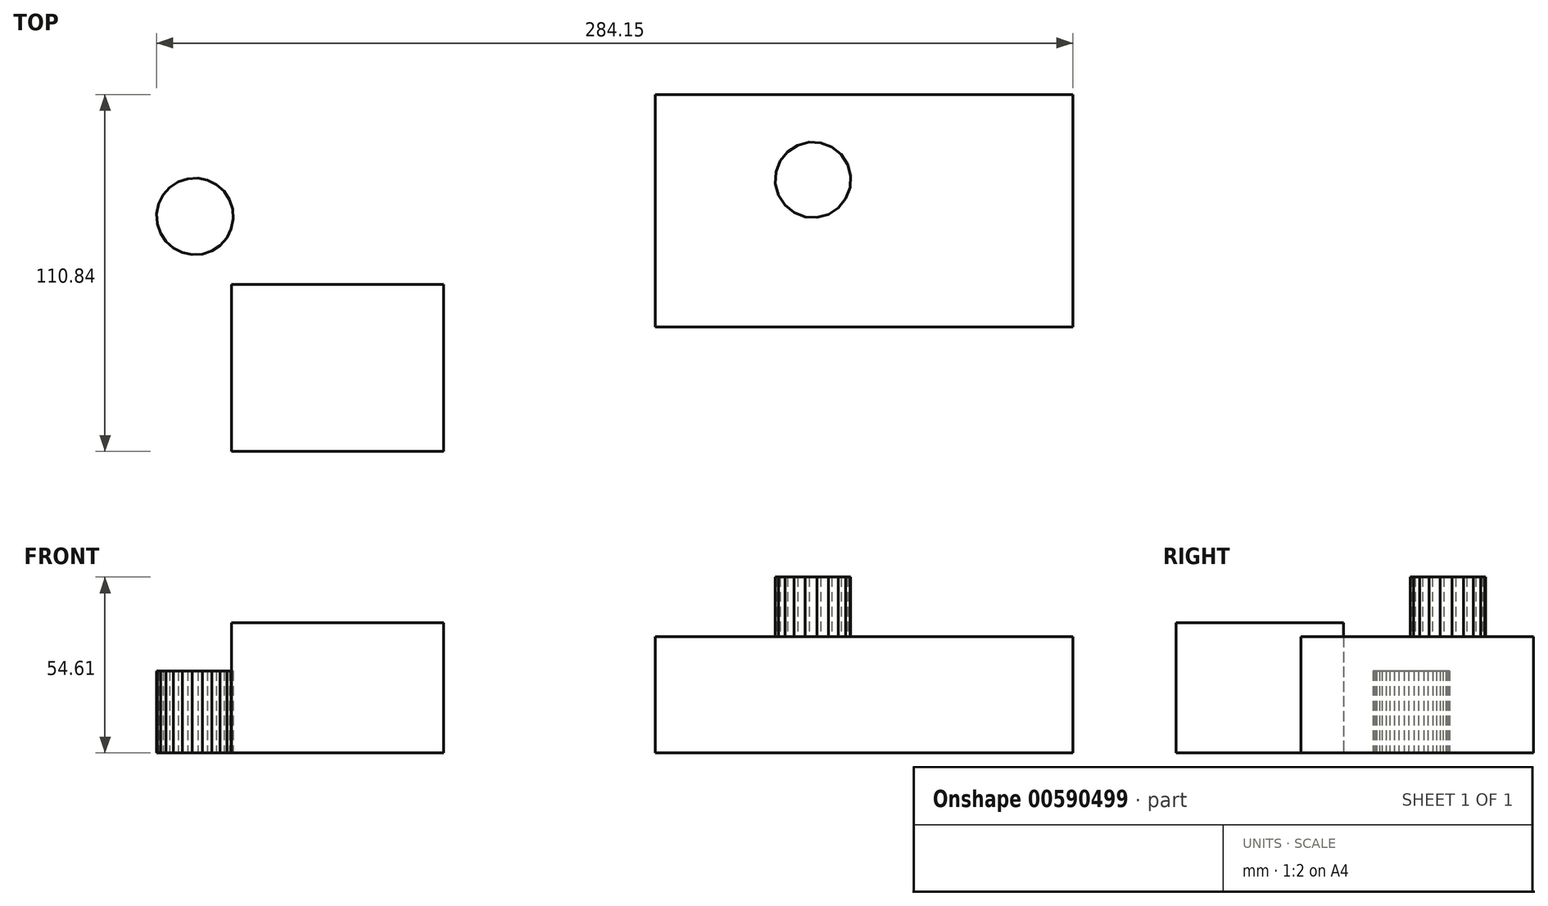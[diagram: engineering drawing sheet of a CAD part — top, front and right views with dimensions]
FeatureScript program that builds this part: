
annotation { "Feature Type Name" : "Feature", "Feature Type Description" : "" }
export const myFeature = defineFeature(function(context is Context, id is Id, definition is map)
    precondition{}
    {
        {
            var Q0;
            Q0=qCreatedBy(makeId("Top.planeOp"),FACE);
            var sketch = newSketch(context, id + "F0", { "sketchPlane" : qUnion([Q0])});
            skLineSegment(sketch, "E0.bottom", {"start": v(-145.28, 51.9) * mm, "end": v(-79.52, 51.9) * mm});
            skLineSegment(sketch, "E0.top", {"start": v(-145.28, 0) * mm, "end": v(-79.52, 0) * mm});
            skLineSegment(sketch, "E0.left", {"start": v(-145.28, 51.9) * mm, "end": v(-145.28, 0) * mm});
            skLineSegment(sketch, "E0.right", {"start": v(-79.52, 51.9) * mm, "end": v(-79.52, 0) * mm});
            skSolve(sketch);
        }
        {
            var Q0;
            Q0 = qSketchRegion(id + "F0", true);
            extrude(context, id + "F1", {"entities" : qUnion([Q0]), "depth" : 40.4 * mm, "offsetDistance" : 25.4 * mm});
        }
        {
            var Q0;
            Q0=qCreatedBy(makeId("Top.planeOp"),FACE);
            var sketch = newSketch(context, id + "F2", { "sketchPlane" : qUnion([Q0])});
            skCircle(sketch, "E1.cCircle", {"center": v(-156.58, 72.97) * mm, "radius": 11.8 * mm, "construction": true});
            skLineSegment(sketch, "E1.0", {"start": v(-146.71, 66.3) * mm, "end": v(-148.78, 63.98) * mm});
            skLineSegment(sketch, "E1.1", {"start": v(-148.78, 63.98) * mm, "end": v(-151.37, 62.26) * mm});
            skLineSegment(sketch, "E1.2", {"start": v(-151.37, 62.26) * mm, "end": v(-154.32, 61.28) * mm});
            skLineSegment(sketch, "E1.3", {"start": v(-154.32, 61.28) * mm, "end": v(-157.42, 61.1) * mm});
            skLineSegment(sketch, "E1.4", {"start": v(-157.42, 61.1) * mm, "end": v(-160.47, 61.72) * mm});
            skLineSegment(sketch, "E1.5", {"start": v(-160.47, 61.72) * mm, "end": v(-163.25, 63.1) * mm});
            skLineSegment(sketch, "E1.6", {"start": v(-163.25, 63.1) * mm, "end": v(-165.57, 65.17) * mm});
            skLineSegment(sketch, "E1.7", {"start": v(-165.57, 65.17) * mm, "end": v(-167.28, 67.76) * mm});
            skLineSegment(sketch, "E1.8", {"start": v(-167.28, 67.76) * mm, "end": v(-168.27, 70.71) * mm});
            skLineSegment(sketch, "E1.9", {"start": v(-168.27, 70.71) * mm, "end": v(-168.45, 73.82) * mm});
            skLineSegment(sketch, "E1.10", {"start": v(-168.45, 73.82) * mm, "end": v(-167.83, 76.86) * mm});
            skLineSegment(sketch, "E1.11", {"start": v(-167.83, 76.86) * mm, "end": v(-166.44, 79.64) * mm});
            skLineSegment(sketch, "E1.12", {"start": v(-166.44, 79.64) * mm, "end": v(-164.38, 81.97) * mm});
            skLineSegment(sketch, "E1.13", {"start": v(-164.38, 81.97) * mm, "end": v(-161.78, 83.68) * mm});
            skLineSegment(sketch, "E1.14", {"start": v(-161.78, 83.68) * mm, "end": v(-158.84, 84.66) * mm});
            skLineSegment(sketch, "E1.15", {"start": v(-158.84, 84.66) * mm, "end": v(-155.73, 84.85) * mm});
            skLineSegment(sketch, "E1.16", {"start": v(-155.73, 84.85) * mm, "end": v(-152.69, 84.23) * mm});
            skLineSegment(sketch, "E1.17", {"start": v(-152.69, 84.23) * mm, "end": v(-149.9, 82.84) * mm});
            skLineSegment(sketch, "E1.18", {"start": v(-149.9, 82.84) * mm, "end": v(-147.58, 80.77) * mm});
            skLineSegment(sketch, "E1.19", {"start": v(-147.58, 80.77) * mm, "end": v(-145.87, 78.18) * mm});
            skLineSegment(sketch, "E1.20", {"start": v(-145.87, 78.18) * mm, "end": v(-144.89, 75.23) * mm});
            skLineSegment(sketch, "E1.21", {"start": v(-144.89, 75.23) * mm, "end": v(-144.7, 72.13) * mm});
            skLineSegment(sketch, "E1.22", {"start": v(-144.7, 72.13) * mm, "end": v(-145.32, 69.08) * mm});
            skLineSegment(sketch, "E1.23", {"start": v(-145.32, 69.08) * mm, "end": v(-146.71, 66.3) * mm});
            skPoint(sketch, "E1.0.midPoint", {"position": v(-147.74, 65.14) * mm});
            skSolve(sketch);
        }
        {
            var Q0;
            Q0 = qSketchRegion(id + "F2", true);
            extrude(context, id + "F3", {"entities" : qUnion([Q0]), "depth" : 25.4 * mm, "offsetDistance" : 25.4 * mm});
        }
        {
            var Q0;
            Q0=qCreatedBy(makeId("Top.planeOp"),FACE);
            var sketch = newSketch(context, id + "F4", { "sketchPlane" : qUnion([Q0])});
            skCircle(sketch, "E2.cCircle", {"center": v(35.11, 84.35) * mm, "radius": 11.58 * mm, "construction": true});
            skLineSegment(sketch, "E2.0", {"start": v(45.27, 78.5) * mm, "end": v(42.96, 75.64) * mm});
            skLineSegment(sketch, "E2.1", {"start": v(42.96, 75.64) * mm, "end": v(39.89, 73.64) * mm});
            skLineSegment(sketch, "E2.2", {"start": v(39.89, 73.64) * mm, "end": v(36.35, 72.7) * mm});
            skLineSegment(sketch, "E2.3", {"start": v(36.35, 72.7) * mm, "end": v(32.68, 72.88) * mm});
            skLineSegment(sketch, "E2.4", {"start": v(32.68, 72.88) * mm, "end": v(29.26, 74.2) * mm});
            skLineSegment(sketch, "E2.5", {"start": v(29.26, 74.2) * mm, "end": v(26.4, 76.5) * mm});
            skLineSegment(sketch, "E2.6", {"start": v(26.4, 76.5) * mm, "end": v(24.4, 79.57) * mm});
            skLineSegment(sketch, "E2.7", {"start": v(24.4, 79.57) * mm, "end": v(23.45, 83.12) * mm});
            skLineSegment(sketch, "E2.8", {"start": v(23.45, 83.12) * mm, "end": v(23.64, 86.78) * mm});
            skLineSegment(sketch, "E2.9", {"start": v(23.64, 86.78) * mm, "end": v(24.96, 90.2) * mm});
            skLineSegment(sketch, "E2.10", {"start": v(24.96, 90.2) * mm, "end": v(27.26, 93.06) * mm});
            skLineSegment(sketch, "E2.11", {"start": v(27.26, 93.06) * mm, "end": v(30.34, 95.06) * mm});
            skLineSegment(sketch, "E2.12", {"start": v(30.34, 95.06) * mm, "end": v(33.88, 96) * mm});
            skLineSegment(sketch, "E2.13", {"start": v(33.88, 96) * mm, "end": v(37.54, 95.82) * mm});
            skLineSegment(sketch, "E2.14", {"start": v(37.54, 95.82) * mm, "end": v(40.97, 94.5) * mm});
            skLineSegment(sketch, "E2.15", {"start": v(40.97, 94.5) * mm, "end": v(43.82, 92.2) * mm});
            skLineSegment(sketch, "E2.16", {"start": v(43.82, 92.2) * mm, "end": v(45.82, 89.13) * mm});
            skLineSegment(sketch, "E2.17", {"start": v(45.82, 89.13) * mm, "end": v(46.77, 85.58) * mm});
            skLineSegment(sketch, "E2.18", {"start": v(46.77, 85.58) * mm, "end": v(46.58, 81.92) * mm});
            skLineSegment(sketch, "E2.19", {"start": v(46.58, 81.92) * mm, "end": v(45.27, 78.5) * mm});
            skPoint(sketch, "E2.0.midPoint", {"position": v(44.12, 77.07) * mm});
            skSolve(sketch);
        }
        {
            var Q0;
            Q0 = qSketchRegion(id + "F4", true);
            extrude(context, id + "F5", {"entities" : qUnion([Q0]), "depth" : 54.6 * mm, "offsetDistance" : 25.4 * mm});
        }
        {
            var Q0;
            Q0=qCreatedBy(makeId("Top.planeOp"),FACE);
            var sketch = newSketch(context, id + "F6", { "sketchPlane" : qUnion([Q0])});
            skLineSegment(sketch, "E3.bottom", {"start": v(-13.78, 110.84) * mm, "end": v(115.7, 110.84) * mm});
            skLineSegment(sketch, "E3.top", {"start": v(-13.78, 38.72) * mm, "end": v(115.7, 38.72) * mm});
            skLineSegment(sketch, "E3.left", {"start": v(-13.78, 110.84) * mm, "end": v(-13.78, 38.72) * mm});
            skLineSegment(sketch, "E3.right", {"start": v(115.7, 110.84) * mm, "end": v(115.7, 38.72) * mm});
            skSolve(sketch);
        }
        {
            var Q0;
            Q0 = qSketchRegion(id + "F6", true);
            extrude(context, id + "F7", {"entities" : qUnion([Q0]), "operationType" : NewBodyOperationType.ADD, "depth" : 36.07 * mm, "offsetDistance" : 25.4 * mm});
        }
    });
